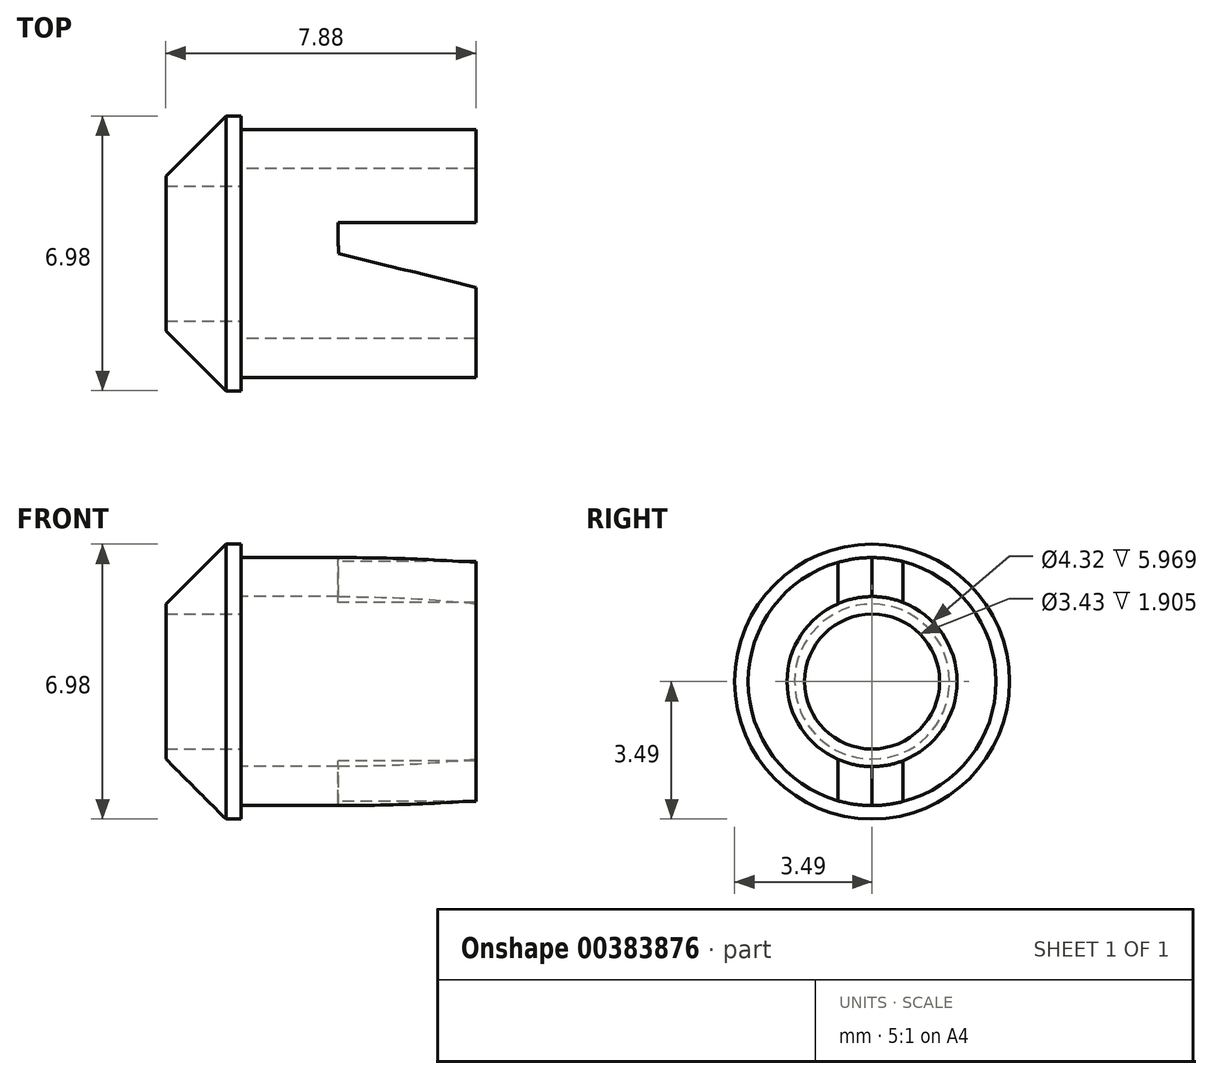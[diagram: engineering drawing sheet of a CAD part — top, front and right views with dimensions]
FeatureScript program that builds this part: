
annotation { "Feature Type Name" : "Feature", "Feature Type Description" : "" }
export const myFeature = defineFeature(function(context is Context, id is Id, definition is map)
    precondition{}
    {
        {
            var Q0;
            Q0=qCreatedBy(makeId("Right.planeOp"),FACE);
            var sketch = newSketch(context, id + "F0", { "sketchPlane" : qUnion([Q0])});
            skCircle(sketch, "E0", {"center": v(0, 0) * mm, "radius": 1.71 * mm});
            skSolve(sketch);
        }
        {
            var Q0;
            Q0=qCreatedBy(makeId("Right.planeOp"),FACE);
            var sketch = newSketch(context, id + "F1", { "sketchPlane" : qUnion([Q0])});
            skCircle(sketch, "E1", {"center": v(0, 0) * mm, "radius": 3.5 * mm});
            skSolve(sketch);
        }
        {
            var Q0;
            Q0=qCreatedBy(makeId("Right.planeOp"),FACE);
            var sketch = newSketch(context, id + "F2", { "sketchPlane" : qUnion([Q0])});
            skCircle(sketch, "E2", {"center": v(0, 0) * mm, "radius": 3.15 * mm});
            skSolve(sketch);
        }
        {
            var Q0;
            Q0=makeQuery(id+"F2.imprint","IMPRINT",FACE,{"disambiguationData":[TD([[makeQuery(id+"F2.imprint","IMPRINT",EDGE,{"derivedFrom":sQuery(id+"F2.wireOp",EDGE,"E2")}),1.0]])]});
            extrude(context, id + "F3", {"entities" : qUnion([Q0]), "depth" : 5.97 * mm});
        }
        {
            var Q0;
            Q0=qCreatedBy(makeId("Right.planeOp"),FACE);
            var sketch = newSketch(context, id + "F4", { "sketchPlane" : qUnion([Q0])});
            skCircle(sketch, "E3", {"center": v(0, 0) * mm, "radius": 2.16 * mm});
            skSolve(sketch);
        }
        {
            var Q0;
            Q0=makeQuery(id+"F4.imprint","IMPRINT",FACE,{"disambiguationData":[TD([[makeQuery(id+"F4.imprint","IMPRINT",EDGE,{"derivedFrom":sQuery(id+"F4.wireOp",EDGE,"E3")}),1.0]])]});
            extrude(context, id + "F5", {"entities" : qUnion([Q0]), "operationType" : NewBodyOperationType.REMOVE, "depth" : 8.97 * mm});
        }
        {
            var Q0;
            Q0=makeQuery(id+"F0.imprint","IMPRINT",FACE,{"disambiguationData":[TD([[makeQuery(id+"F0.imprint","IMPRINT",EDGE,{"derivedFrom":sQuery(id+"F0.wireOp",EDGE,"E0")}),1.0]])]});
            extrude(context, id + "F6", {"entities" : qUnion([Q0]), "operationType" : NewBodyOperationType.REMOVE, "oppositeDirection" : true, "depth" : 3.76 * mm});
        }
        {
            var Q0;
            Q0=qCreatedBy(makeId("Top.planeOp"),FACE);
            var sketch = newSketch(context, id + "F7", { "sketchPlane" : qUnion([Q0])});
            skLineSegment(sketch, "E4", {"start": v(2.46, 0.78) * mm, "end": v(6.6, 0.78) * mm});
            skLineSegment(sketch, "E5", {"start": v(6.6, 0.78) * mm, "end": v(6.6, -1.02) * mm});
            skLineSegment(sketch, "E6", {"start": v(6.6, -1.02) * mm, "end": v(2.48, 0) * mm});
            skLineSegment(sketch, "E7", {"start": v(2.48, 0) * mm, "end": v(2.46, 0.78) * mm});
            skSolve(sketch);
        }
        {
            var Q0;
            Q0=makeQuery(id+"F7.imprint","IMPRINT",FACE,{"disambiguationData":[TD([[makeQuery(id+"F7.imprint","IMPRINT",EDGE,{"derivedFrom":sQuery(id+"F7.wireOp",EDGE,"E4")}),-1.0]])]});
            extrude(context, id + "F8", {"entities" : qUnion([Q0]), "operationType" : NewBodyOperationType.REMOVE, "endBound" : BoundingType.SYMMETRIC, "oppositeDirection" : true, "depth" : 25.4 * mm});
        }
        {
            var Q0;
            Q0=makeQuery(id+"F1.imprint","IMPRINT",FACE,{"disambiguationData":[TD([[makeQuery(id+"F1.imprint","IMPRINT",EDGE,{"derivedFrom":sQuery(id+"F1.wireOp",EDGE,"E1")}),1.0]])]});
            extrude(context, id + "F9", {"entities" : qUnion([Q0]), "operationType" : NewBodyOperationType.ADD, "oppositeDirection" : true, "depth" : 1.9 * mm});
        }
        {
            var Q0;
            Q0 = qSketchRegion(id + "F0", true);
            extrude(context, id + "F10", {"entities" : qUnion([Q0]), "operationType" : NewBodyOperationType.REMOVE, "oppositeDirection" : true, "depth" : 2.54 * mm});
        }
        {
            var Q0;
            Q0=makeQuery(id+"F9.opExtrude","CAP_EDGE",EDGE,{"disambiguationData":[OSD([sQuery(id+"F1.wireOp",EDGE,"E1")])],"isStart":false});
            chamfer(context, id + "F11", {"entities" : qUnion([Q0]), "width" : 1.52 * mm, "tangentPropagation" : true});
        }
    });
